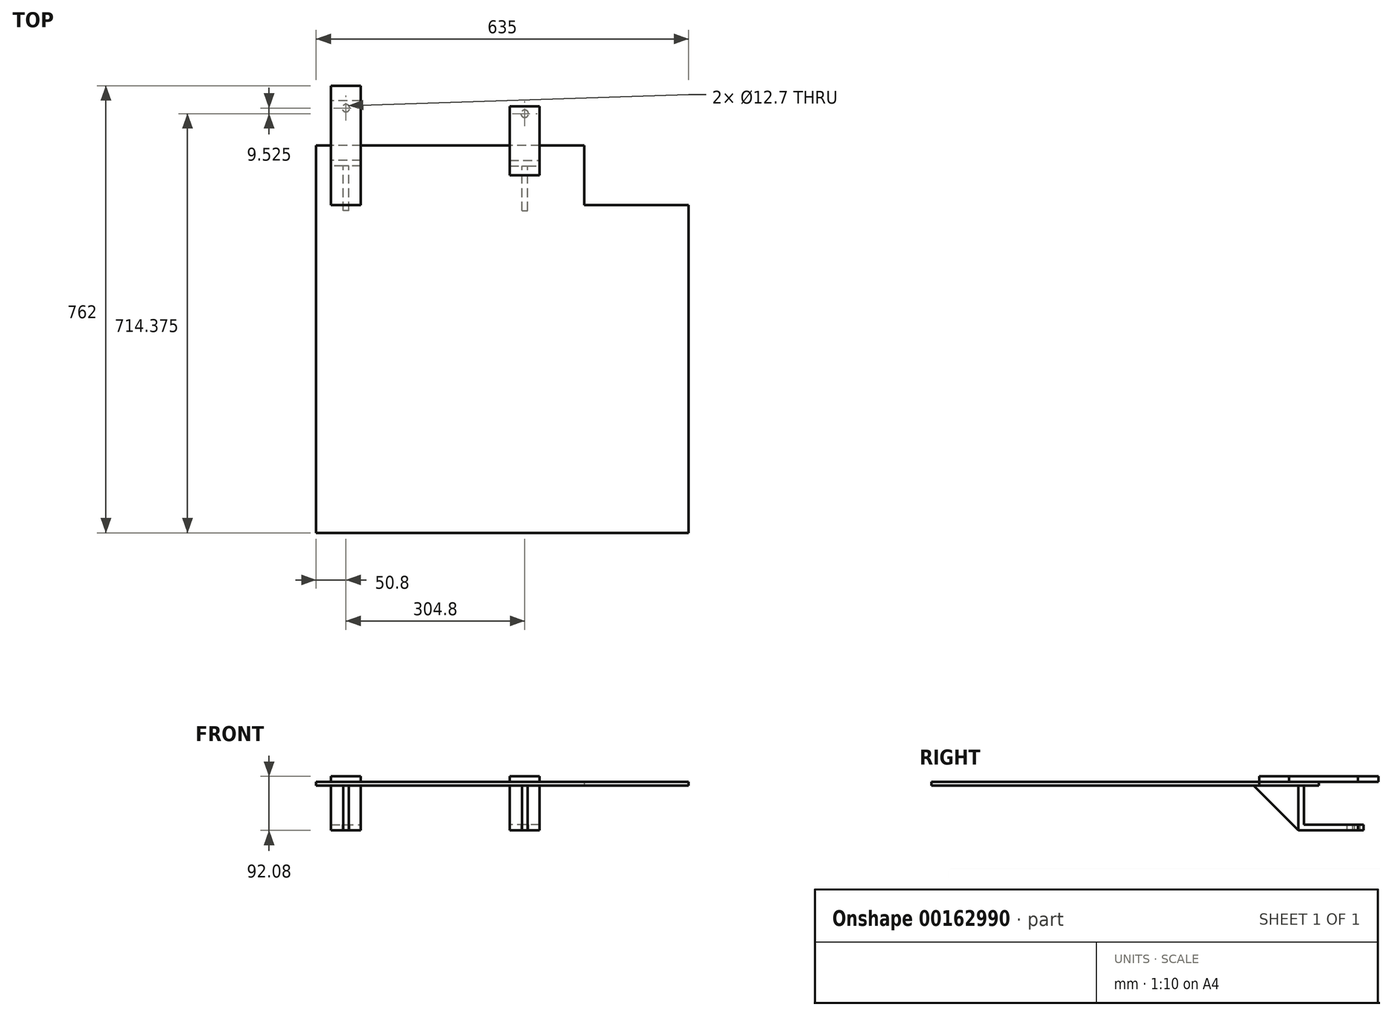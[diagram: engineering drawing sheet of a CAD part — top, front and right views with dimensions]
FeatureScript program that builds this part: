
annotation { "Feature Type Name" : "Feature", "Feature Type Description" : "" }
export const myFeature = defineFeature(function(context is Context, id is Id, definition is map)
    precondition{}
    {
        {
            var Q0;
            Q0=qCreatedBy(makeId("Top.planeOp"),FACE);
            var sketch = newSketch(context, id + "F0", { "sketchPlane" : qUnion([Q0])});
            skLineSegment(sketch, "E0.bottom", {"start": v(317.5, -330.2) * mm, "end": v(-317.5, -330.2) * mm});
            skLineSegment(sketch, "E0.top", {"start": v(139.7, 330.2) * mm, "end": v(-317.5, 330.2) * mm});
            skLineSegment(sketch, "E0.left", {"start": v(317.5, -330.2) * mm, "end": v(317.5, 228.6) * mm});
            skLineSegment(sketch, "E0.right", {"start": v(-317.5, -330.2) * mm, "end": v(-317.5, 330.2) * mm});
            skPoint(sketch, "E0.middle", {"position": v(0, 0) * mm});
            skLineSegment(sketch, "E1.top", {"start": v(317.5, 228.6) * mm, "end": v(139.7, 228.6) * mm});
            skLineSegment(sketch, "E1.right", {"start": v(139.7, 330.2) * mm, "end": v(139.7, 228.6) * mm});
            skPoint(sketch, "E2.orphan", {"position": v(317.5, 330.2) * mm});
            skSolve(sketch);
        }
        {
            var Q0;
            Q0=makeQuery(id+"F0.imprint","IMPRINT",FACE,{"disambiguationData":[TD([[makeQuery(id+"F0.imprint","IMPRINT",EDGE,{"derivedFrom":sQuery(id+"F0.wireOp",EDGE,"E0.bottom")}),-1.0]])]});
            extrude(context, id + "F1", {"entities" : qUnion([Q0]), "depth" : 6.35 * mm});
        }
        {
            var Q0;
            Q0=makeQuery(id+"F1.opExtrude","CAP_FACE",FACE,{"disambiguationData":[OSD([sQuery(id+"F0.wireOp",EDGE,"E0.bottom"),sQuery(id+"F0.wireOp",EDGE,"E0.top"),sQuery(id+"F0.wireOp",EDGE,"E0.left"),sQuery(id+"F0.wireOp",EDGE,"E0.right"),sQuery(id+"F0.wireOp",EDGE,"E1.top"),sQuery(id+"F0.wireOp",EDGE,"E1.right")])],"isStart":false});
            var sketch = newSketch(context, id + "F2", { "sketchPlane" : qUnion([Q0])});
            skLineSegment(sketch, "E3.bottom", {"start": v(-241.3, 228.6) * mm, "end": v(-292.1, 228.6) * mm});
            skLineSegment(sketch, "E3.top", {"start": v(-241.3, 431.8) * mm, "end": v(-292.1, 431.8) * mm});
            skLineSegment(sketch, "E3.left", {"start": v(-241.3, 228.6) * mm, "end": v(-241.3, 431.8) * mm});
            skLineSegment(sketch, "E3.right", {"start": v(-292.1, 228.6) * mm, "end": v(-292.1, 431.8) * mm});
            skPoint(sketch, "E3.middle", {"position": v(-266.7, 330.2) * mm});
            skSolve(sketch);
        }
        {
            var Q0;
            {var subQ0=sQuery(id+"F2.wireOp",EDGE,"E3.bottom");Q0=makeQuery(id+"F2.imprint","IMPRINT",FACE,{"disambiguationData":[TD([[makeQuery(id+"F2.imprint","IMPRINT",EDGE,{"derivedFrom":subQ0}),-1.0]])]});}
            var Q1;
            {var subQ0=sQuery(id+"F2.wireOp",EDGE,"E3.top");Q1=makeQuery(id+"F2.imprint","IMPRINT",FACE,{"disambiguationData":[TD([[makeQuery(id+"F2.imprint","IMPRINT",EDGE,{"derivedFrom":subQ0}),1.0]])]});}
            extrude(context, id + "F3", {"entities" : qUnion([Q0, Q1]), "operationType" : NewBodyOperationType.ADD, "depth" : 9.52 * mm});
        }
        {
            var Q0;
            Q0=makeQuery(id+"F1.opExtrude","CAP_FACE",FACE,{"disambiguationData":[OSD([sQuery(id+"F0.wireOp",EDGE,"E0.bottom"),sQuery(id+"F0.wireOp",EDGE,"E0.top"),sQuery(id+"F0.wireOp",EDGE,"E0.left"),sQuery(id+"F0.wireOp",EDGE,"E0.right"),sQuery(id+"F0.wireOp",EDGE,"E1.top"),sQuery(id+"F0.wireOp",EDGE,"E1.right")])],"isStart":true});
            var sketch = newSketch(context, id + "F4", { "sketchPlane" : qUnion([Q0])});
            skLineSegment(sketch, "E4.bottom", {"start": v(12.7, -295.28) * mm, "end": v(63.5, -295.28) * mm});
            skLineSegment(sketch, "E4.top", {"start": v(12.7, -304.8) * mm, "end": v(63.5, -304.8) * mm});
            skLineSegment(sketch, "E4.left", {"start": v(12.7, -295.28) * mm, "end": v(12.7, -304.8) * mm});
            skLineSegment(sketch, "E4.right", {"start": v(63.5, -295.28) * mm, "end": v(63.5, -304.8) * mm});
            skPoint(sketch, "E4.middle", {"position": v(38.1, -300.04) * mm});
            skSolve(sketch);
        }
        {
            var Q0;
            Q0=makeQuery(id+"F4.imprint","IMPRINT",FACE,{"disambiguationData":[TD([[makeQuery(id+"F4.imprint","IMPRINT",EDGE,{"derivedFrom":sQuery(id+"F4.wireOp",EDGE,"E4.bottom")}),-1.0]])]});
            extrude(context, id + "F5", {"entities" : qUnion([Q0]), "operationType" : NewBodyOperationType.ADD, "depth" : 76.2 * mm});
        }
        {
            var Q0;
            Q0=makeQuery(id+"F5.opExtrude","SWEPT_FACE",FACE,{"disambiguationData":[OSD([sQuery(id+"F4.wireOp",EDGE,"E4.top")])]});
            var sketch = newSketch(context, id + "F6", { "sketchPlane" : qUnion([Q0])});
            skLineSegment(sketch, "E5.bottom", {"start": v(-63.5, -76.2) * mm, "end": v(-12.7, -76.2) * mm});
            skLineSegment(sketch, "E5.top", {"start": v(-63.5, -66.68) * mm, "end": v(-12.7, -66.68) * mm});
            skLineSegment(sketch, "E5.left", {"start": v(-63.5, -76.2) * mm, "end": v(-63.5, -66.68) * mm});
            skLineSegment(sketch, "E5.right", {"start": v(-12.7, -76.2) * mm, "end": v(-12.7, -66.68) * mm});
            skSolve(sketch);
        }
        {
            var Q0;
            Q0=makeQuery(id+"F6.imprint","IMPRINT",FACE,{"disambiguationData":[TD([[makeQuery(id+"F6.imprint","IMPRINT",EDGE,{"derivedFrom":sQuery(id+"F6.wireOp",EDGE,"E5.bottom")}),-1.0]])]});
            extrude(context, id + "F7", {"entities" : qUnion([Q0]), "operationType" : NewBodyOperationType.ADD, "depth" : 92.07 * mm});
        }
        {
            var Q0;
            Q0=makeQuery(id+"F7.boolean.opBoolean","MERGE",FACE,{"derivedFrom":[makeQuery(id+"F5.opExtrude","CAP_FACE",FACE,{"disambiguationData":[OSD([sQuery(id+"F4.wireOp",EDGE,"E4.bottom"),sQuery(id+"F4.wireOp",EDGE,"E4.top"),sQuery(id+"F4.wireOp",EDGE,"E4.left"),sQuery(id+"F4.wireOp",EDGE,"E4.right")])],"isStart":false}),makeQuery(id+"F7.opExtrude","SWEPT_FACE",FACE,{"disambiguationData":[OSD([sQuery(id+"F6.wireOp",EDGE,"E5.bottom")])]})]});
            var sketch = newSketch(context, id + "F8", { "sketchPlane" : qUnion([Q0])});
            skCircle(sketch, "E6", {"center": v(38.1, -384.18) * mm, "radius": 6.35 * mm});
            skPoint(sketch, "E6.centerSnap0", {"position": v(38.1, -396.88) * mm});
            skSolve(sketch);
        }
        {
            var Q0;
            Q0=makeQuery(id+"F8.imprint","IMPRINT",FACE,{"disambiguationData":[TD([[makeQuery(id+"F8.imprint","IMPRINT",EDGE,{"derivedFrom":sQuery(id+"F8.wireOp",EDGE,"E6")}),1.0]])]});
            extrude(context, id + "F9", {"entities" : qUnion([Q0]), "operationType" : NewBodyOperationType.REMOVE, "oppositeDirection" : true, "depth" : 25.4 * mm});
        }
        {
            var Q0;
            Q0=makeQuery(id+"F1.opExtrude","CAP_FACE",FACE,{"disambiguationData":[OSD([sQuery(id+"F0.wireOp",EDGE,"E0.bottom"),sQuery(id+"F0.wireOp",EDGE,"E0.top"),sQuery(id+"F0.wireOp",EDGE,"E0.left"),sQuery(id+"F0.wireOp",EDGE,"E0.right"),sQuery(id+"F0.wireOp",EDGE,"E1.top"),sQuery(id+"F0.wireOp",EDGE,"E1.right")])],"isStart":false});
            var sketch = newSketch(context, id + "F10", { "sketchPlane" : qUnion([Q0])});
            skLineSegment(sketch, "E7.top", {"start": v(63.5, 406.4) * mm, "end": v(12.7, 406.4) * mm});
            skLineSegment(sketch, "E7.left", {"start": v(63.5, 279.4) * mm, "end": v(63.5, 406.4) * mm});
            skLineSegment(sketch, "E7.right", {"start": v(12.7, 279.4) * mm, "end": v(12.7, 406.4) * mm});
            skPoint(sketch, "E7.middle", {"position": v(38.1, 330.2) * mm});
            skLineSegment(sketch, "E8", {"start": v(12.7, 396.88) * mm, "end": v(63.5, 396.88) * mm});
            skLineSegment(sketch, "E9", {"start": v(12.7, 279.4) * mm, "end": v(63.5, 279.4) * mm});
            skPoint(sketch, "E7.bottom.end.orphan", {"position": v(12.7, 254) * mm});
            skPoint(sketch, "E10.orphan", {"position": v(63.5, 254) * mm});
            skPoint(sketch, "E11.orphan", {"position": v(12.7, 330.2) * mm});
            skPoint(sketch, "E12.end.orphan", {"position": v(63.5, 330.2) * mm});
            skSolve(sketch);
        }
        {
            var Q0;
            {var subQ0=sQuery(id+"F10.wireOp",EDGE,"E8");Q0=makeQuery(id+"F10.imprint","IMPRINT",FACE,{"disambiguationData":[TD([[makeQuery(id+"F10.imprint","IMPRINT",EDGE,{"derivedFrom":subQ0}),-1.0]])]});}
            var Q1;
            {var subQ0=sQuery(id+"F10.wireOp",EDGE,"E9");Q1=makeQuery(id+"F10.imprint","IMPRINT",FACE,{"disambiguationData":[TD([[makeQuery(id+"F10.imprint","IMPRINT",EDGE,{"derivedFrom":subQ0}),1.0]])]});}
            extrude(context, id + "F11", {"entities" : qUnion([Q0, Q1]), "operationType" : NewBodyOperationType.ADD, "depth" : 9.52 * mm});
        }
        {
            var Q0;
            Q0=makeQuery(id+"F5.opExtrude","SWEPT_FACE",FACE,{"disambiguationData":[OSD([sQuery(id+"F4.wireOp",EDGE,"E4.bottom")])]});
            var sketch = newSketch(context, id + "F12", { "sketchPlane" : qUnion([Q0])});
            skLineSegment(sketch, "E13.bottom", {"start": v(33.34, 0) * mm, "end": v(42.86, 0) * mm});
            skLineSegment(sketch, "E13.top", {"start": v(33.34, -152.4) * mm, "end": v(42.86, -152.4) * mm});
            skLineSegment(sketch, "E13.left", {"start": v(33.34, 0) * mm, "end": v(33.34, -76.2) * mm});
            skLineSegment(sketch, "E13.right", {"start": v(42.86, 0) * mm, "end": v(42.86, -76.2) * mm});
            skPoint(sketch, "E13.middle", {"position": v(38.1, -76.2) * mm});
            skLineSegment(sketch, "E14", {"start": v(42.86, -76.2) * mm, "end": v(33.34, -76.2) * mm});
            skSolve(sketch);
        }
        {
            var Q0;
            Q0 = qSketchRegion(id + "F12", true);
            extrude(context, id + "F13", {"entities" : qUnion([Q0]), "operationType" : NewBodyOperationType.ADD, "depth" : 76.2 * mm});
        }
        {
            var Q0;
            Q0=makeQuery(id+"F13.opExtrude","SWEPT_FACE",FACE,{"disambiguationData":[OSD([sQuery(id+"F12.wireOp",EDGE,"E13.right")])]});
            var sketch = newSketch(context, id + "F14", { "sketchPlane" : qUnion([Q0])});
            skLineSegment(sketch, "E15", {"start": v(295.28, -76.2) * mm, "end": v(219.08, 0) * mm});
            skLineSegment(sketch, "E16", {"start": v(295.28, -76.2) * mm, "end": v(219.08, -76.2) * mm});
            skLineSegment(sketch, "E17", {"start": v(219.08, -76.2) * mm, "end": v(219.08, 0) * mm});
            skSolve(sketch);
        }
        {
            var Q0;
            Q0 = qSketchRegion(id + "F14", true);
            extrude(context, id + "F15", {"entities" : qUnion([Q0]), "operationType" : NewBodyOperationType.REMOVE, "oppositeDirection" : true, "depth" : 25.4 * mm});
        }
        {
            var Q0;
            Q0=makeQuery(id+"F1.opExtrude","CAP_FACE",FACE,{"disambiguationData":[OSD([sQuery(id+"F0.wireOp",EDGE,"E0.bottom"),sQuery(id+"F0.wireOp",EDGE,"E0.top"),sQuery(id+"F0.wireOp",EDGE,"E0.left"),sQuery(id+"F0.wireOp",EDGE,"E0.right"),sQuery(id+"F0.wireOp",EDGE,"E1.top"),sQuery(id+"F0.wireOp",EDGE,"E1.right")])],"isStart":true});
            var sketch = newSketch(context, id + "F16", { "sketchPlane" : qUnion([Q0])});
            skLineSegment(sketch, "E18.bottom", {"start": v(-241.3, -304.8) * mm, "end": v(-292.1, -304.8) * mm});
            skLineSegment(sketch, "E18.top", {"start": v(-241.3, -295.28) * mm, "end": v(-292.1, -295.28) * mm});
            skLineSegment(sketch, "E18.left", {"start": v(-241.3, -304.8) * mm, "end": v(-241.3, -295.28) * mm});
            skLineSegment(sketch, "E18.right", {"start": v(-292.1, -304.8) * mm, "end": v(-292.1, -295.28) * mm});
            skSolve(sketch);
        }
        {
            var Q0;
            Q0=makeQuery(id+"F16.imprint","IMPRINT",FACE,{"disambiguationData":[TD([[makeQuery(id+"F16.imprint","IMPRINT",EDGE,{"derivedFrom":sQuery(id+"F16.wireOp",EDGE,"E18.bottom")}),-1.0]])]});
            extrude(context, id + "F17", {"entities" : qUnion([Q0]), "operationType" : NewBodyOperationType.ADD, "depth" : 76.2 * mm});
        }
        {
            var Q0;
            Q0=makeQuery(id+"F17.opExtrude","SWEPT_FACE",FACE,{"disambiguationData":[OSD([sQuery(id+"F16.wireOp",EDGE,"E18.bottom")])]});
            var sketch = newSketch(context, id + "F18", { "sketchPlane" : qUnion([Q0])});
            skLineSegment(sketch, "E19.bottom", {"start": v(292.1, -76.2) * mm, "end": v(241.3, -76.2) * mm});
            skLineSegment(sketch, "E19.top", {"start": v(292.1, -66.67) * mm, "end": v(241.3, -66.67) * mm});
            skLineSegment(sketch, "E19.left", {"start": v(292.1, -76.2) * mm, "end": v(292.1, -66.67) * mm});
            skLineSegment(sketch, "E19.right", {"start": v(241.3, -76.2) * mm, "end": v(241.3, -66.67) * mm});
            skSolve(sketch);
        }
        {
            var Q0;
            Q0 = qSketchRegion(id + "F18", true);
            extrude(context, id + "F19", {"entities" : qUnion([Q0]), "operationType" : NewBodyOperationType.ADD, "depth" : 101.6 * mm});
        }
        {
            var Q0;
            Q0=makeQuery(id+"F19.boolean.opBoolean","MERGE",FACE,{"derivedFrom":[makeQuery(id+"F17.opExtrude","CAP_FACE",FACE,{"disambiguationData":[OSD([sQuery(id+"F16.wireOp",EDGE,"E18.bottom"),sQuery(id+"F16.wireOp",EDGE,"E18.top"),sQuery(id+"F16.wireOp",EDGE,"E18.left"),sQuery(id+"F16.wireOp",EDGE,"E18.right")])],"isStart":false}),makeQuery(id+"F19.opExtrude","SWEPT_FACE",FACE,{"disambiguationData":[OSD([sQuery(id+"F18.wireOp",EDGE,"E19.bottom")])]})]});
            var sketch = newSketch(context, id + "F20", { "sketchPlane" : qUnion([Q0])});
            skCircle(sketch, "E20", {"center": v(-266.7, -393.7) * mm, "radius": 6.35 * mm});
            skPoint(sketch, "E20.centerSnap0", {"position": v(-266.7, -406.4) * mm});
            skSolve(sketch);
        }
        {
            var Q0;
            Q0=makeQuery(id+"F20.imprint","IMPRINT",FACE,{"disambiguationData":[TD([[makeQuery(id+"F20.imprint","IMPRINT",EDGE,{"derivedFrom":sQuery(id+"F20.wireOp",EDGE,"E20")}),1.0]])]});
            extrude(context, id + "F21", {"entities" : qUnion([Q0]), "operationType" : NewBodyOperationType.REMOVE, "oppositeDirection" : true, "depth" : 25.4 * mm});
        }
        {
            var Q0;
            Q0=makeQuery(id+"F17.opExtrude","SWEPT_FACE",FACE,{"disambiguationData":[OSD([sQuery(id+"F16.wireOp",EDGE,"E18.top")])]});
            var sketch = newSketch(context, id + "F22", { "sketchPlane" : qUnion([Q0])});
            skLineSegment(sketch, "E21.bottom", {"start": v(-261.94, 0) * mm, "end": v(-271.46, 0) * mm});
            skLineSegment(sketch, "E21.left", {"start": v(-261.94, 0) * mm, "end": v(-261.94, -76.2) * mm});
            skLineSegment(sketch, "E21.right", {"start": v(-271.46, 0) * mm, "end": v(-271.46, -76.2) * mm});
            skPoint(sketch, "E21.middle", {"position": v(-266.7, -76.2) * mm});
            skLineSegment(sketch, "E22", {"start": v(-271.46, -76.2) * mm, "end": v(-261.94, -76.2) * mm});
            skPoint(sketch, "E21.top.start.orphan", {"position": v(-261.94, -152.4) * mm});
            skPoint(sketch, "E23.orphan", {"position": v(-271.46, -152.4) * mm});
            skSolve(sketch);
        }
        {
            var Q0;
            Q0 = qSketchRegion(id + "F22", true);
            extrude(context, id + "F23", {"entities" : qUnion([Q0]), "operationType" : NewBodyOperationType.ADD, "depth" : 76.2 * mm});
        }
        {
            var Q0;
            Q0=makeQuery(id+"F23.opExtrude","SWEPT_FACE",FACE,{"disambiguationData":[OSD([sQuery(id+"F22.wireOp",EDGE,"E21.right")])]});
            var sketch = newSketch(context, id + "F24", { "sketchPlane" : qUnion([Q0])});
            skLineSegment(sketch, "E24", {"start": v(-295.28, -76.2) * mm, "end": v(-219.08, 0) * mm});
            skLineSegment(sketch, "E25", {"start": v(-219.08, 0) * mm, "end": v(-219.08, -76.2) * mm});
            skLineSegment(sketch, "E26", {"start": v(-219.08, -76.2) * mm, "end": v(-295.28, -76.2) * mm});
            skSolve(sketch);
        }
        {
            var Q0;
            Q0 = qSketchRegion(id + "F24", true);
            extrude(context, id + "F25", {"entities" : qUnion([Q0]), "operationType" : NewBodyOperationType.REMOVE, "oppositeDirection" : true, "depth" : 25.4 * mm});
        }
    });
